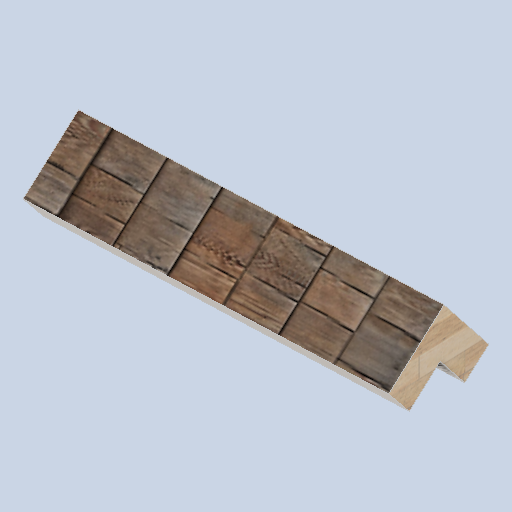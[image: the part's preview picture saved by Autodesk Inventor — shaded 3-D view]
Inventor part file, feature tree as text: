
AUTODESK INVENTOR PART (.ipt)
format: ipt  version: 2024.2 (Build 282272000, 272)  size: 240,128 bytes
history: native  units: in
note: dims shown in document units (in); Inventor stores cm internally (conversion verified against a paired STEP export)
features: sketch x8, plane x5, other x3
ambient origin geometry x8: Origin, YZ Plane, XZ Plane, XY Plane, X Axis, Y Axis, Z Axis, Center Point
bodies: Solid1 (feature_tree)
feature tree (16):
  other  "panel_pad_frame_02_MIR.ipt"
  other  "Solid1::panel_pad_frame_02_MIR.ipt"
  other  "TaggingFeature1"
  sketch  "Sketch1"  dims[d0=0.3937in]
  sketch  "Sketch2"
  sketch  "Sketch3"
  sketch  "Sketch6"
  sketch  "Sketch7"
  sketch  "Sketch8"
  sketch  "Sketch9"
  sketch  "Sketch10"
  plane  "Work Plane1"
  plane  "Work Plane2"
  plane  "Work Plane3"
  plane  "Work Plane4"
  plane  "Work Plane5"
